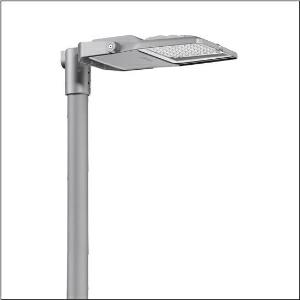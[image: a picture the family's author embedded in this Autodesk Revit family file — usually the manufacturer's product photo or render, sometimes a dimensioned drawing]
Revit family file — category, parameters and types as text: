
# Revit family: floodlight_fl_21_iq_mini___pl43_5xa7772d4a3a_0702
name_source: partatom
category: Lighting Fixtures
units: mm (PartAtom-declared; Revit-internal decimal feet)

## family parameters
Cut with Voids When Loaded = No
Host = Face
Light Source = No
Part Type = Normal
Room Calculation Point = No
Round Connector Dimension = Use Diameter
Shared = No

## types (1)
- --- (1 x LED, 19090 lm, 143 W, 4000K)
    Apparent Load = 143 VA
    CIE Flux Codes = 27 78 99 100 100
    Color Rendering = 70
    Color Temperature = 4000K
    Default Elevation = 1800 mm
    Description = Floodlight FL 21 iQ mini, floodlight, primary light control with lens, of PMMA, primary optical cover: protective disc, of toughened safety glass, transparent, light distribution: PL43, light emission: direct distribution, installation type: surface-mounted, LED, High Power LED, rated luminous flux: 19.090lm, luminous efficacy: 134lm/W, light colour: 740, colour temperature: 4000K, control: Auto-Match, Temp-Guard, Night-Set, Smart-Wire, Desk-Remote (wireless, voltage-free reading and setting of iQ features in the workshop via application-optimized NFC function/RFID function), optimised constant luminous flux control (CLO 2.0), Light-Fading, Lumen-Switch, with terminal, 6-pole, mains connection: 220..240V, AC, 50/60Hz, start of lifetime: 143W, end of service life: 152W, reduction: 61W, luminaire housing, of diecast aluminium, powder-coated, Siteco® metallic grey (DB 702S), corrosivity category C5 mid according to DIN EN ISO 12944, sealing non-destructively replaceable, please order mast flange separately, mast bracket, of steel, galvanised, powder-coated, protection rating (complete): IP66, insulation class (complete): insulation class II (safety insulation), certification: CE, ENEC, VDE, protection symbol: D, impact resistance: IK08, permissible operating ambient temperature: -40..+40°C, permissible operating ambient temperature for outdoor applications: -40..+50°C, standard: DIN EN 12944, LABS conformity tested according to VDMA 24364:2018-05, packaging unit: 1 piece

Light Distribution: PL43
    Height = 70 mm
    Lamp = 1 x LED
    Lamp Light Flux = 19090 lm
    Lamp Power = 143 W
    Lamp count = 1
    Length = 485 mm
    Luminous efficacy = 133 lm/W
    Manufacturer = Siteco
    ModVariant = No
    Model = 5XA7772D4A3A
    Number of Poles = 1
    OnlyDefault = Yes
    Power Factor = 1
    Product Name = Floodlight FL 21 iQ mini | PL43
    Product group = floodlight | pylon annexe
    ProductGroupID = 6200
    Protection Class = Protection class II
    Protection Degree = IP 66
    RLX_Detail_Level = 1
    RLX_Emergency_Light_Flux = 0 lm
    RLX_Emergency_Type = 0
    RLX_Emergency_Type_DB = No
    RlxData = <blob elided: 101577 chars, md5=04248387>
    Socket = socket
    Standby Power = 0 W
    System Light Flux = 19090 lm
    System Power = 143 W
    Type Comments = factory setting: luminous flux: 100 % | dim-lin: 254 | 730 mA
    Type Image = l_1007125.jpg
    URL = http://relux.com
    VarID = @adj_093773
    Voltage = 0 V
    Weight = 0.00 kg
    Width = 337 mm

## geometry (parser evidence)
native form markers: Blend x4, Sweep x12
no freeform markers — native parametric forms only
